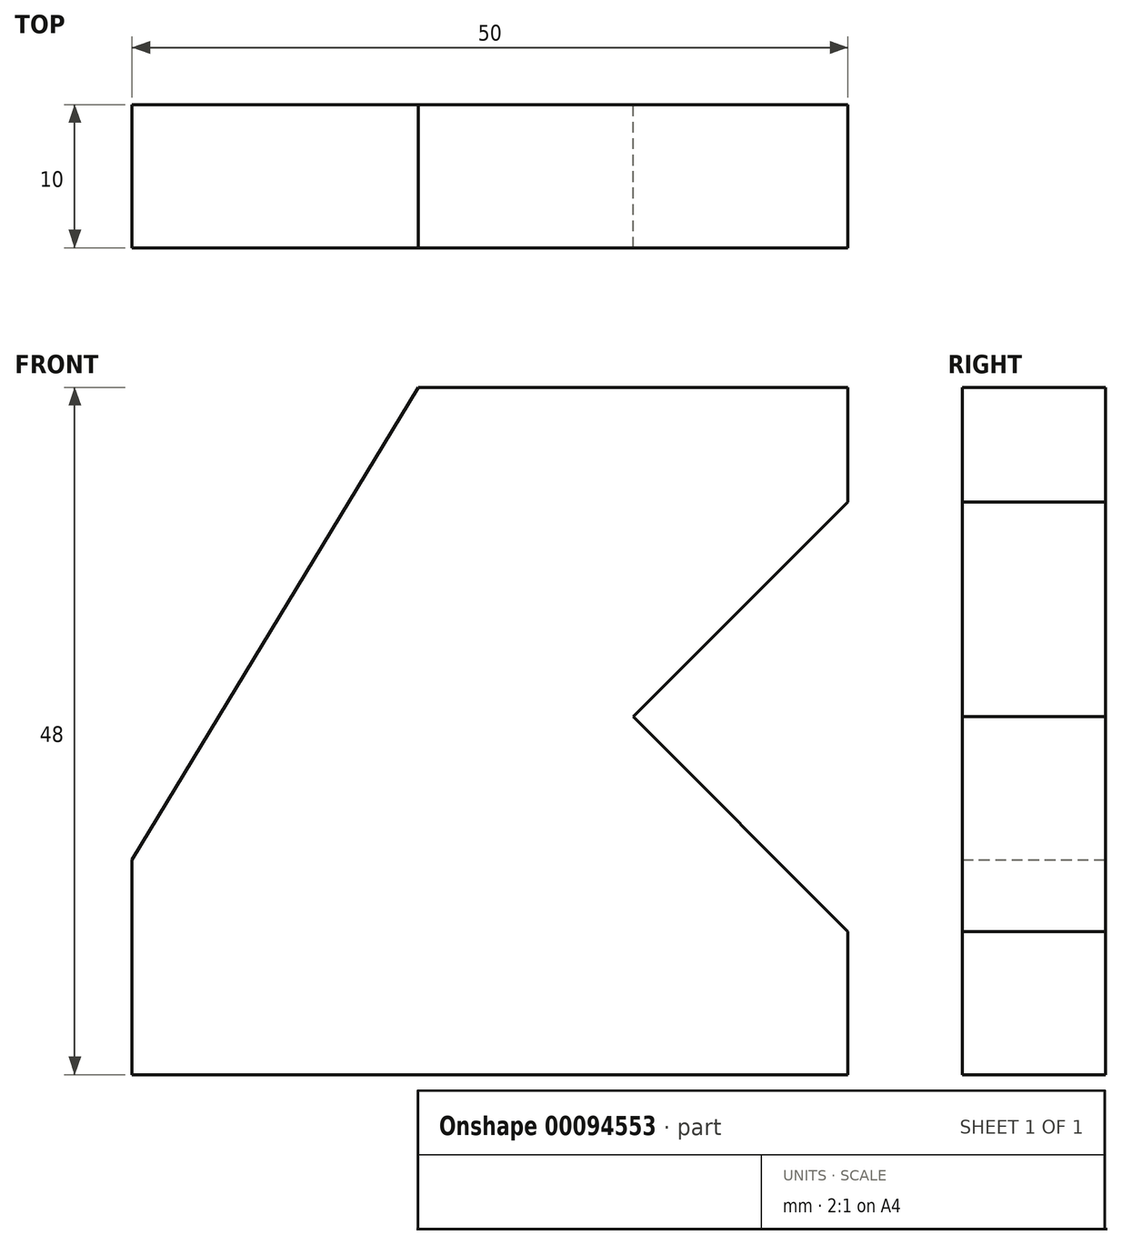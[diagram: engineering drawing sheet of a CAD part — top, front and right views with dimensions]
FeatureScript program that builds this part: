
annotation { "Feature Type Name" : "Feature", "Feature Type Description" : "" }
export const myFeature = defineFeature(function(context is Context, id is Id, definition is map)
    precondition{}
    {
        {
            var Q0;
            Q0=qCreatedBy(makeId("Front.planeOp"),FACE);
            var sketch = newSketch(context, id + "F0", { "sketchPlane" : qUnion([Q0])});
            skLineSegment(sketch, "E0", {"start": v(0, 0) * mm, "end": v(50, 0) * mm});
            skLineSegment(sketch, "E1", {"start": v(0, 0) * mm, "end": v(0, 15) * mm});
            skLineSegment(sketch, "E2", {"start": v(50, 0) * mm, "end": v(50, 10) * mm});
            skLineSegment(sketch, "E3", {"start": v(50, 48) * mm, "end": v(20, 48) * mm});
            skLineSegment(sketch, "E4", {"start": v(0, 15) * mm, "end": v(20, 48) * mm});
            skLineSegment(sketch, "E5", {"start": v(35, 25) * mm, "end": v(50, 10) * mm});
            skLineSegment(sketch, "E6", {"start": v(35, 25) * mm, "end": v(50, 40) * mm});
            skLineSegment(sketch, "E7.trimOffspring", {"start": v(50, 40) * mm, "end": v(50, 48) * mm});
            skSolve(sketch);
        }
        {
            var Q0;
            Q0 = qSketchRegion(id + "F0", true);
            extrude(context, id + "F1", {"entities" : qUnion([Q0]), "depth" : 10 * mm});
        }
    });
